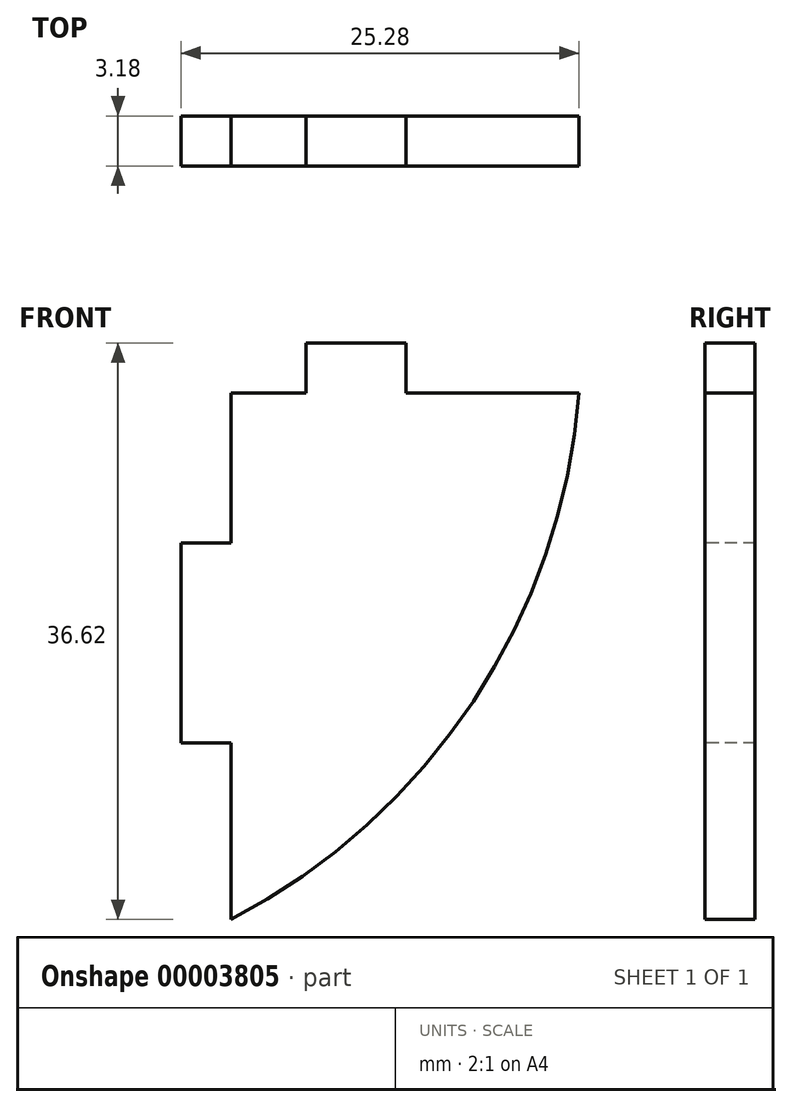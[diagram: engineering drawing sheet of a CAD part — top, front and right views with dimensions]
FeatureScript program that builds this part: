
annotation { "Feature Type Name" : "Feature", "Feature Type Description" : "" }
export const myFeature = defineFeature(function(context is Context, id is Id, definition is map)
    precondition{}
    {
        {
            var Q0;
            Q0=qCreatedBy(makeId("Front.planeOp"),FACE);
            var sketch = newSketch(context, id + "F0", { "sketchPlane" : qUnion([Q0])});
            skLineSegment(sketch, "E0.bottom", {"start": v(0, 0) * mm, "end": v(25.4, 0) * mm});
            skLineSegment(sketch, "E0.top", {"start": v(0, 38.1) * mm, "end": v(25.4, 38.1) * mm});
            skLineSegment(sketch, "E0.left", {"start": v(0, 0) * mm, "end": v(0, 38.1) * mm});
            skLineSegment(sketch, "E0.right", {"start": v(25.4, 0) * mm, "end": v(25.4, 38.1) * mm});
            skSolve(sketch);
        }
        {
            var Q0;
            Q0 = qSketchRegion(id + "F0", true);
            extrude(context, id + "F1", {"entities" : qUnion([Q0]), "oppositeDirection" : true, "depth" : 3.17 * mm});
        }
        {
            var Q0;
            Q0=makeQuery(id+"F1.opExtrude","CAP_FACE",FACE,{"disambiguationData":[OSD([sQuery(id+"F0.wireOp",EDGE,"E0.bottom"),sQuery(id+"F0.wireOp",EDGE,"E0.top"),sQuery(id+"F0.wireOp",EDGE,"E0.left"),sQuery(id+"F0.wireOp",EDGE,"E0.right")])],"isStart":true});
            var sketch = newSketch(context, id + "F2", { "sketchPlane" : qUnion([Q0])});
            skArc(sketch, "E1", {"start": v(0, 0) * mm, "mid": v(18.47, 15.2) * mm, "end": v(25.4, 38.1) * mm});
            skLineSegment(sketch, "E2", {"start": v(25.4, 38.1) * mm, "end": v(25.4, 0) * mm});
            skLineSegment(sketch, "E3", {"start": v(25.4, 0) * mm, "end": v(0, 0) * mm});
            skSolve(sketch);
        }
        {
            var Q0;
            Q0 = qSketchRegion(id + "F2", true);
            extrude(context, id + "F3", {"entities" : qUnion([Q0]), "operationType" : NewBodyOperationType.REMOVE, "oppositeDirection" : true, "depth" : 25.4 * mm});
        }
        {
            var Q0;
            Q0=makeQuery(id+"F1.opExtrude","CAP_FACE",FACE,{"disambiguationData":[OSD([sQuery(id+"F0.wireOp",EDGE,"E0.bottom"),sQuery(id+"F0.wireOp",EDGE,"E0.top"),sQuery(id+"F0.wireOp",EDGE,"E0.left"),sQuery(id+"F0.wireOp",EDGE,"E0.right")])],"isStart":true});
            var sketch = newSketch(context, id + "F4", { "sketchPlane" : qUnion([Q0])});
            skLineSegment(sketch, "E4.bottom", {"start": v(0, 38.1) * mm, "end": v(3.17, 38.1) * mm});
            skLineSegment(sketch, "E4.top", {"start": v(0, 25.4) * mm, "end": v(3.18, 25.4) * mm});
            skLineSegment(sketch, "E4.left", {"start": v(0, 38.1) * mm, "end": v(0, 25.4) * mm});
            skLineSegment(sketch, "E4.right", {"start": v(3.18, 38.1) * mm, "end": v(3.18, 25.4) * mm});
            skLineSegment(sketch, "E5", {"start": v(0, 19.05) * mm, "end": v(31.09, 19.05) * mm, "construction": true});
            skLineSegment(sketch, "E6.0.MirrorCS", {"start": v(3.18, 0) * mm, "end": v(3.18, 12.7) * mm});
            skLineSegment(sketch, "E7.0.MirrorCS", {"start": v(0, 0) * mm, "end": v(3.17, 0) * mm});
            skLineSegment(sketch, "E8.0.MirrorCS", {"start": v(0, 0) * mm, "end": v(0, 12.7) * mm});
            skLineSegment(sketch, "E9.0.MirrorCS", {"start": v(0, 12.7) * mm, "end": v(3.18, 12.7) * mm});
            skLineSegment(sketch, "E10.bottom", {"start": v(3.17, 38.1) * mm, "end": v(7.94, 38.1) * mm});
            skLineSegment(sketch, "E10.top", {"start": v(3.18, 34.93) * mm, "end": v(7.94, 34.93) * mm});
            skLineSegment(sketch, "E10.left", {"start": v(3.17, 38.1) * mm, "end": v(3.17, 34.93) * mm});
            skLineSegment(sketch, "E10.right", {"start": v(7.94, 38.1) * mm, "end": v(7.94, 34.93) * mm});
            skLineSegment(sketch, "E11.bottom", {"start": v(14.29, 38.1) * mm, "end": v(25.4, 38.1) * mm});
            skLineSegment(sketch, "E11.top", {"start": v(14.29, 34.93) * mm, "end": v(25.4, 34.93) * mm});
            skLineSegment(sketch, "E11.left", {"start": v(14.29, 38.1) * mm, "end": v(14.29, 34.93) * mm});
            skLineSegment(sketch, "E11.right", {"start": v(25.4, 38.1) * mm, "end": v(25.4, 34.93) * mm});
            skSolve(sketch);
        }
        {
            var Q0;
            Q0 = qSketchRegion(id + "F4", true);
            extrude(context, id + "F5", {"entities" : qUnion([Q0]), "operationType" : NewBodyOperationType.REMOVE, "endBound" : BoundingType.THROUGH_ALL, "oppositeDirection" : true, "depth" : 53.68 * mm});
        }
    });
